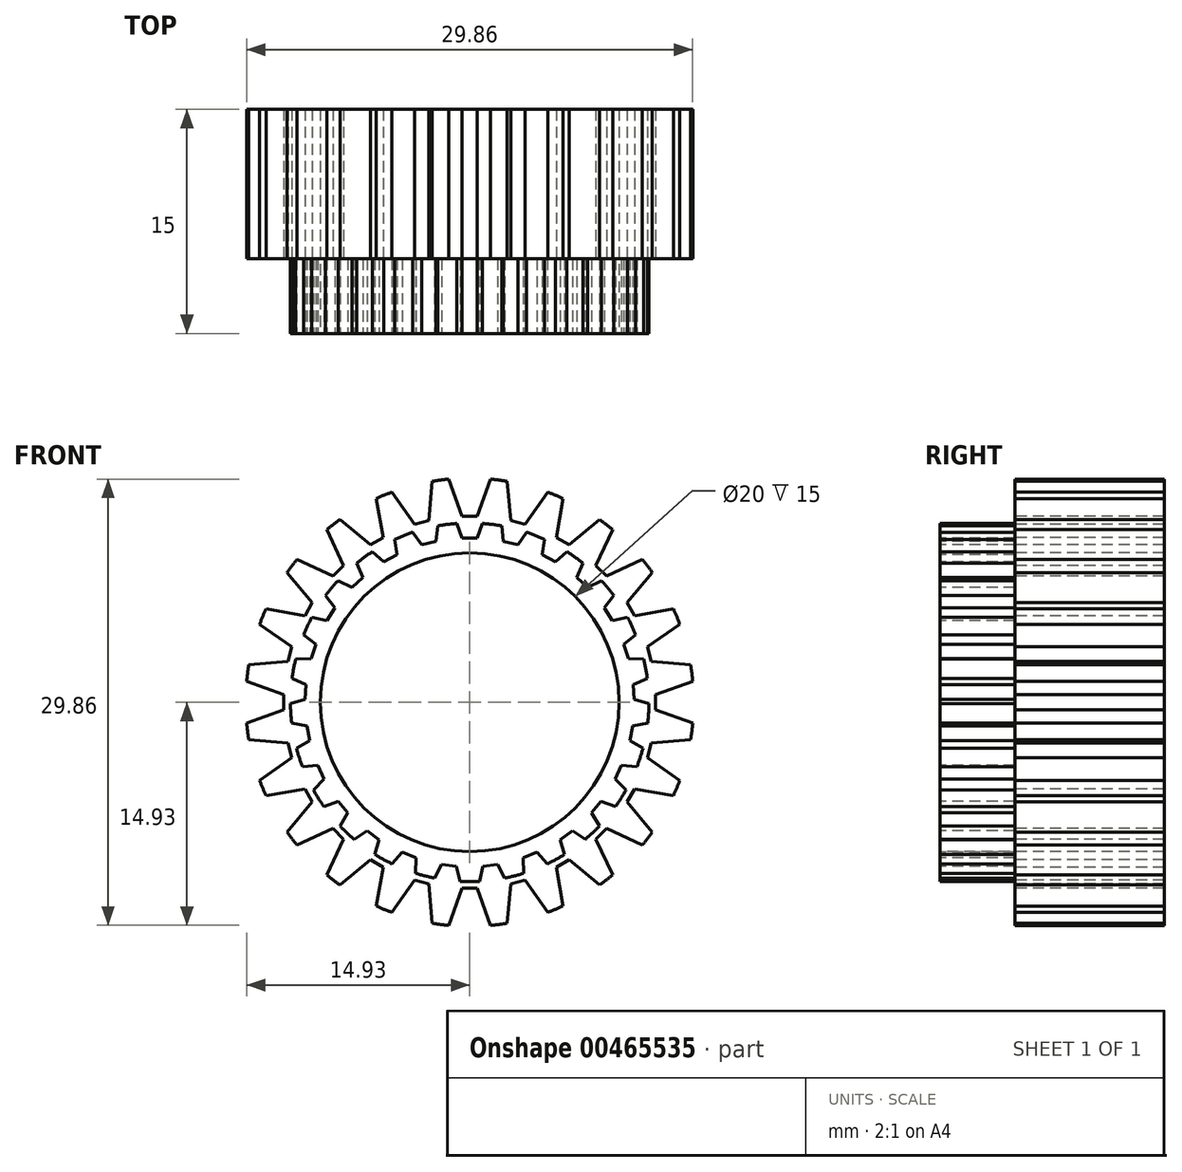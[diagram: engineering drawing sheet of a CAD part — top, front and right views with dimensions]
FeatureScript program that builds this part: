
annotation { "Feature Type Name" : "Feature", "Feature Type Description" : "" }
export const myFeature = defineFeature(function(context is Context, id is Id, definition is map)
    precondition{}
    {
        {
            var Q0;
            Q0=qCreatedBy(makeId("Front.planeOp"),FACE);
            var sketch = newSketch(context, id + "F0", { "sketchPlane" : qUnion([Q0])});
            skCircle(sketch, "E0", {"center": v(0, 0) * mm, "radius": 10 * mm});
            skCircle(sketch, "E1", {"center": v(0, 0) * mm, "radius": 15 * mm});
            skSolve(sketch);
        }
        {
            var Q0;
            Q0=makeQuery(id+"F0.imprint","IMPRINT",FACE,{"disambiguationData":[TD([[makeQuery(id+"F0.imprint","IMPRINT",EDGE,{"derivedFrom":sQuery(id+"F0.wireOp",EDGE,"E0")}),-1.0]])]});
            extrude(context, id + "F1", {"entities" : qUnion([Q0]), "oppositeDirection" : true, "depth" : 10 * mm});
        }
        {
            var Q0;
            Q0=makeQuery(id+"F1.opExtrude","CAP_FACE",FACE,{"disambiguationData":[OSD([sQuery(id+"F0.wireOp",EDGE,"E0"),sQuery(id+"F0.wireOp",EDGE,"E1")])],"isStart":true});
            var sketch = newSketch(context, id + "F2", { "sketchPlane" : qUnion([Q0])});
            skLineSegment(sketch, "E2", {"start": v(0, 0) * mm, "end": v(0, 15) * mm, "construction": true});
            skLineSegment(sketch, "E3", {"start": v(0, 12.45) * mm, "end": v(-0.5, 12.45) * mm});
            skLineSegment(sketch, "E4", {"start": v(0, 12.45) * mm, "end": v(0.5, 12.45) * mm});
            skLineSegment(sketch, "E5", {"start": v(-0.5, 12.45) * mm, "end": v(-1.4, 14.93) * mm});
            skLineSegment(sketch, "E6", {"start": v(0.5, 12.45) * mm, "end": v(1.4, 14.93) * mm});
            skCircle(sketch, "E7", {"center": v(0, 0) * mm, "radius": 12 * mm});
            skSolve(sketch);
        }
        {
            var Q0;
            Q0=makeQuery(id+"F2.imprint","IMPRINT",FACE,{"disambiguationData":[TD([[makeQuery(id+"F2.imprint","IMPRINT",EDGE,{"derivedFrom":sQuery(id+"F2.wireOp",EDGE,"E3")}),-1.0]])]});
            extrude(context, id + "F3", {"entities" : qUnion([Q0]), "operationType" : NewBodyOperationType.REMOVE, "oppositeDirection" : true, "depth" : 25 * mm});
        }
        {
            var Q0;
            Q0=makeQuery(id+"F3.boolean.opBoolean","COPY",FACE,{"derivedFrom":makeQuery(id+"F3.opExtrude","SWEPT_FACE",FACE,{"disambiguationData":[OSD([sQuery(id+"F2.wireOp",EDGE,"E5")])]})});
            var Q1;
            Q1=makeQuery(id+"F3.boolean.opBoolean","COPY",FACE,{"derivedFrom":makeQuery(id+"F3.opExtrude","SWEPT_FACE",FACE,{"disambiguationData":[OSD([sQuery(id+"F2.wireOp",EDGE,"E3"),sQuery(id+"F2.wireOp",EDGE,"E4")])]})});
            var Q2;
            Q2=makeQuery(id+"F3.boolean.opBoolean","COPY",FACE,{"derivedFrom":makeQuery(id+"F3.opExtrude","SWEPT_FACE",FACE,{"disambiguationData":[OSD([sQuery(id+"F2.wireOp",EDGE,"E6")])]})});
            var Q3;
            Q3=makeQuery(id+"F1.opExtrude","SWEPT_FACE",FACE,{"disambiguationData":[OSD([sQuery(id+"F0.wireOp",EDGE,"E1")])]});
            circularPattern(context, id + "F4", {"patternType" : PatternType.FACE, "faces" : qUnion([Q0, Q1, Q2]), "axis" : qUnion([Q3]), "angle" : 360 * degree, "instanceCount" : 24, "equalSpace" : true});
        }
        {
            var Q0;
            Q0 = qSketchRegion(id + "F2", true);
            extrude(context, id + "F5", {"entities" : qUnion([Q0]), "operationType" : NewBodyOperationType.ADD, "depth" : 5 * mm});
        }
        {
            var Q0;
            Q0=makeQuery(id+"F5.opExtrude","CAP_FACE",FACE,{"disambiguationData":[OSD([sQuery(id+"F2.wireOp",EDGE,"E7")])],"isStart":false});
            var sketch = newSketch(context, id + "F6", { "sketchPlane" : qUnion([Q0])});
            skCircle(sketch, "E8", {"center": v(0, 0) * mm, "radius": 10 * mm});
            skLineSegment(sketch, "E9", {"start": v(0, 0) * mm, "end": v(0, 12) * mm, "construction": true});
            skLineSegment(sketch, "E10", {"start": v(0, 11) * mm, "end": v(0, 12) * mm, "construction": true});
            skLineSegment(sketch, "E11", {"start": v(0, 11) * mm, "end": v(-0.5, 11) * mm});
            skLineSegment(sketch, "E12", {"start": v(0, 11) * mm, "end": v(0.5, 11) * mm});
            skLineSegment(sketch, "E13", {"start": v(-0.5, 11) * mm, "end": v(-0.85, 11.97) * mm});
            skLineSegment(sketch, "E14", {"start": v(0.5, 11) * mm, "end": v(0.85, 11.97) * mm});
            skSolve(sketch);
        }
        {
            var Q0;
            Q0=makeQuery(id+"F6.imprint","IMPRINT",FACE,{"disambiguationData":[TD([[makeQuery(id+"F6.imprint","IMPRINT",EDGE,{"derivedFrom":sQuery(id+"F6.wireOp",EDGE,"E8")}),1.0]])]});
            extrude(context, id + "F7", {"entities" : qUnion([Q0]), "operationType" : NewBodyOperationType.REMOVE, "oppositeDirection" : true, "depth" : 25 * mm});
        }
        {
            var Q0;
            Q0=makeQuery(id+"F6.imprint","IMPRINT",FACE,{"disambiguationData":[TD([[makeQuery(id+"F6.imprint","IMPRINT",EDGE,{"derivedFrom":sQuery(id+"F6.wireOp",EDGE,"E11")}),-1.0]])]});
            extrude(context, id + "F8", {"entities" : qUnion([Q0]), "operationType" : NewBodyOperationType.REMOVE, "oppositeDirection" : true, "depth" : 5 * mm});
        }
        {
            var Q0;
            Q0=makeQuery(id+"F8.boolean.opBoolean","COPY",FACE,{"derivedFrom":makeQuery(id+"F8.opExtrude","SWEPT_FACE",FACE,{"disambiguationData":[OSD([sQuery(id+"F6.wireOp",EDGE,"E13")])]})});
            var Q1;
            Q1=makeQuery(id+"F8.boolean.opBoolean","COPY",FACE,{"derivedFrom":makeQuery(id+"F8.opExtrude","SWEPT_FACE",FACE,{"disambiguationData":[OSD([sQuery(id+"F6.wireOp",EDGE,"E11"),sQuery(id+"F6.wireOp",EDGE,"E12")])]})});
            var Q2;
            Q2=makeQuery(id+"F8.boolean.opBoolean","COPY",FACE,{"derivedFrom":makeQuery(id+"F8.opExtrude","SWEPT_FACE",FACE,{"disambiguationData":[OSD([sQuery(id+"F6.wireOp",EDGE,"E14")])]})});
            var Q3;
            Q3=makeQuery(id+"F5.opExtrude","SWEPT_FACE",FACE,{"disambiguationData":[OSD([sQuery(id+"F2.wireOp",EDGE,"E7")])]});
            circularPattern(context, id + "F9", {"patternType" : PatternType.FACE, "faces" : qUnion([Q0, Q1, Q2]), "axis" : qUnion([Q3]), "angle" : 360 * degree, "instanceCount" : 25, "equalSpace" : true});
        }
    });
